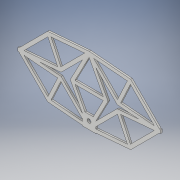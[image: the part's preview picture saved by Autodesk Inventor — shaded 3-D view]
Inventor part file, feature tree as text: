
AUTODESK INVENTOR PART (.ipt)
format: ipt  version: 2018 (Build 220112000, 112)  size: 231,424 bytes
history: native  units: in
note: dims shown in document units (in); Inventor stores cm internally (conversion verified against a paired STEP export)
features: extrude x1, sketch x1
ambient origin geometry x8: Origin, YZ Plane, XZ Plane, XY Plane, X Axis, Y Axis, Z Axis, Center Point
bodies: Body1 (feature_tree)
feature tree (2):
  extrude  "Extrusion3"  Depth=0.125in
  sketch  "Sketch1"  dims[d1=10.5in d2=5.0in d4=45.0deg d6=0.0327in d7=1.2041in d9=0.0327in d10=2.5in d11=5.25in d12=0.125in d13=135.0deg d14=0.125in d16=135.0deg d17=0.125in d18=2.5in d19=1.2041in d20=45.0deg d21=45.0deg d22=1.25in d23=1.25in d24=2.375in d25=5.25in d26=0.125in d32=0.5in d33=4.75in d34=1.0in d37=0.5583in d38=0.2791in d45=0.25in d46=0.125in d47=0.125in d48=0.125in d49=0.125in d50=0.125in d51=0.125in d54=0.25in d55=0.25in d56=0.25in d57=0.125in d76=0.125in d77=1.043in d78=0.25in d83=0.0327in d84=0.0327in d85=45.0deg d86=0.0327in d87=0.0327in d88=0.4277in d89=0.977in d90=0.1517in d91=1.0in d92=0.0417in d95=0.25in d96=0.25in d97=0.125in d98=0.125in d99=0.25in d100=0.25in d101=45.0deg d102=0.25in d103=0.25in d104=0.125in d105=0.0in]
